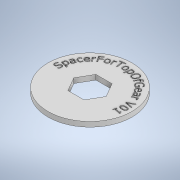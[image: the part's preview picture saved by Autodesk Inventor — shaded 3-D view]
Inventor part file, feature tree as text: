
AUTODESK INVENTOR PART (.ipt)
format: ipt  version: 2022.2 (Build 262287000, 287)  size: 607,232 bytes
history: native  units: in
note: dims shown in document units (in); Inventor stores cm internally (conversion verified against a paired STEP export)
features: sketch x2, extrude x1, emboss x1
ambient origin geometry x8: Origin, YZ Plane, XZ Plane, XY Plane, X Axis, Y Axis, Z Axis, Center Point
bodies: Solid1 (feature_tree)
feature tree (4):
  extrude  "Extrusion1"  Depth=1.0in
  emboss  "Emboss1"
  sketch  "Sketch1"  dims[d0=3.0in d1=1.0in]
  sketch  "Sketch2"  dims[d2=0.175in d3=0.0in d4=2.5in d5=0.05in d6=0.0in]
